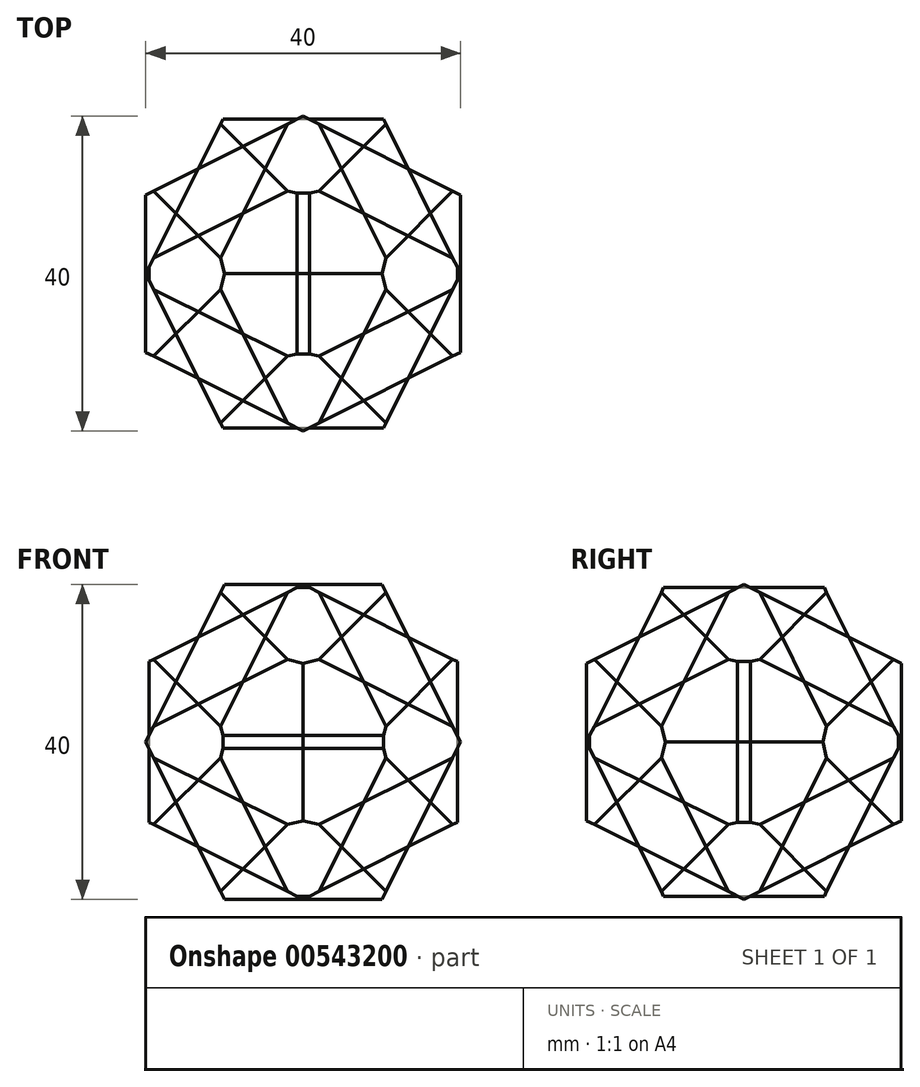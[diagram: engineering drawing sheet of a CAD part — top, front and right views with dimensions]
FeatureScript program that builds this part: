
annotation { "Feature Type Name" : "Feature", "Feature Type Description" : "" }
export const myFeature = defineFeature(function(context is Context, id is Id, definition is map)
    precondition{}
    {
        {
            var Q0;
            Q0=qCreatedBy(makeId("Front.planeOp"),FACE);
            var sketch = newSketch(context, id + "F0", { "sketchPlane" : qUnion([Q0])});
            skLineSegment(sketch, "E0", {"start": v(40, 0) * mm, "end": v(0, 20) * mm});
            skLineSegment(sketch, "E1", {"start": v(0, 20) * mm, "end": v(-40, 0) * mm});
            skLineSegment(sketch, "E2", {"start": v(-40, 0) * mm, "end": v(0, -20) * mm});
            skLineSegment(sketch, "E3", {"start": v(0, -20) * mm, "end": v(40, 0) * mm});
            skSolve(sketch);
        }
        {
            var Q0;
            Q0=makeQuery(id+"F0.imprint","IMPRINT",FACE,{"disambiguationData":[TD([[makeQuery(id+"F0.imprint","IMPRINT",EDGE,{"derivedFrom":sQuery(id+"F0.wireOp",EDGE,"E0")}),1.0]])]});
            extrude(context, id + "F1", {"entities" : qUnion([Q0]), "depth" : 25 * mm, "offsetDistance" : 25 * mm, "hasSecondDirection" : true, "secondDirectionOppositeDirection" : true, "secondDirectionDepth" : 25 * mm});
        }
        {
            var Q0;
            Q0=qCreatedBy(makeId("Front.planeOp"),FACE);
            var sketch = newSketch(context, id + "F2", { "sketchPlane" : qUnion([Q0])});
            skLineSegment(sketch, "E4", {"start": v(0, 49.78) * mm, "end": v(0, 0) * mm});
            skSolve(sketch);
        }
        {
            var Q0;
            Q0=qCreatedBy(makeId("Front.planeOp"),FACE);
            var sketch = newSketch(context, id + "F3", { "sketchPlane" : qUnion([Q0])});
            skLineSegment(sketch, "E5", {"start": v(60.84, 0) * mm, "end": v(0, 0) * mm});
            skSolve(sketch);
        }
        {
            var Q0;
            Q0=qCreatedBy(makeId("Right.planeOp"),FACE);
            var sketch = newSketch(context, id + "F4", { "sketchPlane" : qUnion([Q0])});
            skLineSegment(sketch, "E6", {"start": v(48.72, 0) * mm, "end": v(-1.84, 0) * mm});
            skSolve(sketch);
        }
        {
            var Q0;
            Q0=makeQuery(id+"F1.opExtrude","SWEPT_BODY",BODY,{"disambiguationData":[OSD([sQuery(id+"F0.wireOp",EDGE,"E0"),sQuery(id+"F0.wireOp",EDGE,"E1"),sQuery(id+"F0.wireOp",EDGE,"E2"),sQuery(id+"F0.wireOp",EDGE,"E3")])]});
            var Q1;
            Q1=sQuery(id+"F2.wireOp",EDGE,"E4");
            transform(context, id + "F5", {"entities" : qUnion([Q0]), "transformType" : TransformType.ROTATION, "transformAxis" : qUnion([Q1]), "angle" : 90 * degree, "makeCopy" : true});
        }
        {
            var Q0;
            Q0=makeQuery(id+"F5.opPattern","COPY",BODY,{"derivedFrom":makeQuery(id+"F1.opExtrude","SWEPT_BODY",BODY,{"disambiguationData":[OSD([sQuery(id+"F0.wireOp",EDGE,"E0"),sQuery(id+"F0.wireOp",EDGE,"E1"),sQuery(id+"F0.wireOp",EDGE,"E2"),sQuery(id+"F0.wireOp",EDGE,"E3")])]}),"instanceName":"1"});
            var Q1;
            Q1=sQuery(id+"F4.wireOp",EDGE,"E6");
            transform(context, id + "F6", {"entities" : qUnion([Q0]), "transformType" : TransformType.ROTATION, "transformAxis" : qUnion([Q1]), "angle" : 90 * degree, "makeCopy" : true});
        }
        {
            var Q0;
            Q0=makeQuery(id+"F5.opPattern","COPY",BODY,{"derivedFrom":makeQuery(id+"F1.opExtrude","SWEPT_BODY",BODY,{"disambiguationData":[OSD([sQuery(id+"F0.wireOp",EDGE,"E0"),sQuery(id+"F0.wireOp",EDGE,"E1"),sQuery(id+"F0.wireOp",EDGE,"E2"),sQuery(id+"F0.wireOp",EDGE,"E3")])]}),"instanceName":"1"});
            var Q1;
            Q1=sQuery(id+"F3.wireOp",EDGE,"E5");
            transform(context, id + "F7", {"entities" : qUnion([Q0]), "transformType" : TransformType.ROTATION, "transformAxis" : qUnion([Q1]), "angle" : 90 * degree, "makeCopy" : false});
        }
        {
            var Q0;
            Q0=makeQuery(id+"F5.opPattern","COPY",BODY,{"derivedFrom":makeQuery(id+"F1.opExtrude","SWEPT_BODY",BODY,{"disambiguationData":[OSD([sQuery(id+"F0.wireOp",EDGE,"E0"),sQuery(id+"F0.wireOp",EDGE,"E1"),sQuery(id+"F0.wireOp",EDGE,"E2"),sQuery(id+"F0.wireOp",EDGE,"E3")])]}),"instanceName":"1"});
            var Q1;
            Q1=makeQuery(id+"F6.opPattern","COPY",BODY,{"derivedFrom":makeQuery(id+"F5.opPattern","COPY",BODY,{"derivedFrom":makeQuery(id+"F1.opExtrude","SWEPT_BODY",BODY,{"disambiguationData":[OSD([sQuery(id+"F0.wireOp",EDGE,"E0"),sQuery(id+"F0.wireOp",EDGE,"E1"),sQuery(id+"F0.wireOp",EDGE,"E2"),sQuery(id+"F0.wireOp",EDGE,"E3")])]}),"instanceName":"1"}),"instanceName":"1"});
            booleanBodies(context, id + "F8", {"operationType" : BooleanOperationType.INTERSECTION, "tools" : qUnion([Q0, Q1])});
        }
        {
            var Q0;
            {var subQ0=makeQuery(id+"F5.opPattern","COPY",BODY,{"derivedFrom":makeQuery(id+"F1.opExtrude","SWEPT_BODY",BODY,{"disambiguationData":[OSD([sQuery(id+"F0.wireOp",EDGE,"E0"),sQuery(id+"F0.wireOp",EDGE,"E1"),sQuery(id+"F0.wireOp",EDGE,"E2"),sQuery(id+"F0.wireOp",EDGE,"E3")])]}),"instanceName":"1"});Q0=makeQuery(id+"F8.opBoolean","INTERSECT",BODY,{"derivedFrom":[subQ0,makeQuery(id+"F6.opPattern","COPY",BODY,{"derivedFrom":subQ0,"instanceName":"1"})]});}
            var Q1;
            Q1=makeQuery(id+"F1.opExtrude","SWEPT_BODY",BODY,{"disambiguationData":[OSD([sQuery(id+"F0.wireOp",EDGE,"E0"),sQuery(id+"F0.wireOp",EDGE,"E1"),sQuery(id+"F0.wireOp",EDGE,"E2"),sQuery(id+"F0.wireOp",EDGE,"E3")])]});
            booleanBodies(context, id + "F9", {"operationType" : BooleanOperationType.INTERSECTION, "tools" : qUnion([Q0, Q1])});
        }
        {
            var Q0;
            Q0=qCreatedBy(makeId("Top.planeOp"),FACE);
            var sketch = newSketch(context, id + "F10", { "sketchPlane" : qUnion([Q0])});
            skLineSegment(sketch, "E7", {"start": v(20, 0) * mm, "end": v(0, 20) * mm});
            skLineSegment(sketch, "E8", {"start": v(0, 20) * mm, "end": v(-20, 0) * mm});
            skLineSegment(sketch, "E9", {"start": v(-20, 0) * mm, "end": v(0, -20) * mm});
            skLineSegment(sketch, "E10", {"start": v(0, -20) * mm, "end": v(20, 0) * mm});
            skSolve(sketch);
        }
        {
            var Q0;
            Q0=qSketchRegion(id+"F10",true);
            extrude(context, id + "F11", {"entities" : qUnion([Q0]), "depth" : 20 * mm, "offsetDistance" : 25 * mm, "hasDraft" : true, "draftAngle" : atan(1 / sqrt(2)), "draftPullDirection" : true, "hasSecondDirection" : true, "secondDirectionOppositeDirection" : true, "secondDirectionDepth" : 20 * mm, "hasSecondDirectionDraft" : true, "secondDirectionDraftAngle" : atan(1 / sqrt(2)), "secondDirectionDraftPullDirection" : true});
        }
        {
            var Q0;
            {var subQ0=makeQuery(id+"F1.opExtrude","SWEPT_BODY",BODY,{"disambiguationData":[OSD([sQuery(id+"F0.wireOp",EDGE,"E0"),sQuery(id+"F0.wireOp",EDGE,"E1"),sQuery(id+"F0.wireOp",EDGE,"E2"),sQuery(id+"F0.wireOp",EDGE,"E3")])]});var subQ1=makeQuery(id+"F5.opPattern","COPY",BODY,{"derivedFrom":subQ0,"instanceName":"1"});Q0=makeQuery(id+"F9.opBoolean","INTERSECT",BODY,{"derivedFrom":[subQ0,makeQuery(id+"F8.opBoolean","INTERSECT",BODY,{"derivedFrom":[subQ1,makeQuery(id+"F6.opPattern","COPY",BODY,{"derivedFrom":subQ1,"instanceName":"1"})]})]});}
            transform(context, id + "F12", {"entities" : qUnion([Q0]), "transformType" : TransformType.TRANSLATION_3D, "dx" : 50 * mm, "dy" : 0 * mm, "dz" : 0 * mm, "makeCopy" : false});
        }
        {
            var Q0;
            Q0=makeQuery(id+"F11.*.split.splitOp","SPLIT",BODY,{"derivedFrom":makeQuery(id+"F11.opExtrude","SWEPT_BODY",BODY,{"disambiguationData":[OSD([sQuery(id+"F10.wireOp",EDGE,"E7"),sQuery(id+"F10.wireOp",EDGE,"E8"),sQuery(id+"F10.wireOp",EDGE,"E9"),sQuery(id+"F10.wireOp",EDGE,"E10")])]})});
            var Q1;
            Q1=qCreatedBy(makeId("Origin.pointOp"),VERTEX);
            transform(context, id + "F13", {"entities" : qUnion([Q0]), "transformType" : TransformType.SCALE_UNIFORMLY, "scale" : 1.5, "scalePoint" : qUnion([Q1]), "makeCopy" : false});
        }
        {
            var Q0;
            {var subQ0=makeQuery(id+"F1.opExtrude","SWEPT_BODY",BODY,{"disambiguationData":[OSD([sQuery(id+"F0.wireOp",EDGE,"E0"),sQuery(id+"F0.wireOp",EDGE,"E1"),sQuery(id+"F0.wireOp",EDGE,"E2"),sQuery(id+"F0.wireOp",EDGE,"E3")])]});var subQ1=makeQuery(id+"F5.opPattern","COPY",BODY,{"derivedFrom":subQ0,"instanceName":"1"});Q0=makeQuery(id+"F9.opBoolean","INTERSECT",BODY,{"derivedFrom":[subQ0,makeQuery(id+"F8.opBoolean","INTERSECT",BODY,{"derivedFrom":[subQ1,makeQuery(id+"F6.opPattern","COPY",BODY,{"derivedFrom":subQ1,"instanceName":"1"})]})]});}
            transform(context, id + "F14", {"entities" : qUnion([Q0]), "transformType" : TransformType.TRANSLATION_3D, "dx" : -50 * mm, "dy" : 0 * mm, "dz" : 0 * mm, "makeCopy" : false});
        }
        {
            var Q0;
            Q0=makeQuery(id+"F11.*.split.splitOp","SPLIT",BODY,{"derivedFrom":makeQuery(id+"F11.opExtrude","SWEPT_BODY",BODY,{"disambiguationData":[OSD([sQuery(id+"F10.wireOp",EDGE,"E7"),sQuery(id+"F10.wireOp",EDGE,"E8"),sQuery(id+"F10.wireOp",EDGE,"E9"),sQuery(id+"F10.wireOp",EDGE,"E10")])]})});
            var Q1;
            Q1=qCreatedBy(makeId("Origin.pointOp"),VERTEX);
            transform(context, id + "F15", {"entities" : qUnion([Q0]), "transformType" : TransformType.SCALE_UNIFORMLY, "scale" : 1.05, "scalePoint" : qUnion([Q1]), "makeCopy" : false});
        }
        {
            var Q0;
            Q0=makeQuery(id+"F11.*.split.splitOp","SPLIT",BODY,{"derivedFrom":makeQuery(id+"F11.opExtrude","SWEPT_BODY",BODY,{"disambiguationData":[OSD([sQuery(id+"F10.wireOp",EDGE,"E7"),sQuery(id+"F10.wireOp",EDGE,"E8"),sQuery(id+"F10.wireOp",EDGE,"E9"),sQuery(id+"F10.wireOp",EDGE,"E10")])]})});
            var Q1;
            {var subQ0=makeQuery(id+"F1.opExtrude","SWEPT_BODY",BODY,{"disambiguationData":[OSD([sQuery(id+"F0.wireOp",EDGE,"E0"),sQuery(id+"F0.wireOp",EDGE,"E1"),sQuery(id+"F0.wireOp",EDGE,"E2"),sQuery(id+"F0.wireOp",EDGE,"E3")])]});var subQ1=makeQuery(id+"F5.opPattern","COPY",BODY,{"derivedFrom":subQ0,"instanceName":"1"});Q1=makeQuery(id+"F9.opBoolean","INTERSECT",BODY,{"derivedFrom":[subQ0,makeQuery(id+"F8.opBoolean","INTERSECT",BODY,{"derivedFrom":[subQ1,makeQuery(id+"F6.opPattern","COPY",BODY,{"derivedFrom":subQ1,"instanceName":"1"})]})]});}
            booleanBodies(context, id + "F16", {"operationType" : BooleanOperationType.INTERSECTION, "tools" : qUnion([Q0, Q1])});
        }
        {
            var Q0;
            {var subQ0=makeQuery(id+"F1.opExtrude","SWEPT_BODY",BODY,{"disambiguationData":[OSD([sQuery(id+"F0.wireOp",EDGE,"E0"),sQuery(id+"F0.wireOp",EDGE,"E1"),sQuery(id+"F0.wireOp",EDGE,"E2"),sQuery(id+"F0.wireOp",EDGE,"E3")])]});var subQ1=makeQuery(id+"F5.opPattern","COPY",BODY,{"derivedFrom":subQ0,"instanceName":"1"});Q0=makeQuery(id+"F16.opBoolean","INTERSECT",BODY,{"derivedFrom":[makeQuery(id+"F9.opBoolean","INTERSECT",BODY,{"derivedFrom":[subQ0,makeQuery(id+"F8.opBoolean","INTERSECT",BODY,{"derivedFrom":[subQ1,makeQuery(id+"F6.opPattern","COPY",BODY,{"derivedFrom":subQ1,"instanceName":"1"})]})]}),makeQuery(id+"F11.*.split.splitOp","SPLIT",BODY,{"derivedFrom":makeQuery(id+"F11.opExtrude","SWEPT_BODY",BODY,{"disambiguationData":[OSD([sQuery(id+"F10.wireOp",EDGE,"E7"),sQuery(id+"F10.wireOp",EDGE,"E8"),sQuery(id+"F10.wireOp",EDGE,"E9"),sQuery(id+"F10.wireOp",EDGE,"E10")])]})})]});}
            var Q1;
            Q1=sQuery(id+"F2.wireOp",EDGE,"E4");
            transform(context, id + "F17", {"entities" : qUnion([Q0]), "transformType" : TransformType.ROTATION, "transformAxis" : qUnion([Q1]), "angle" : 90 * degree, "makeCopy" : true});
        }
        {
            var Q0;
            Q0=qCreatedBy(makeId("Top.planeOp"),FACE);
            var sketch = newSketch(context, id + "F18", { "sketchPlane" : qUnion([Q0])});
            skLineSegment(sketch, "E11", {"start": v(-20, -20) * mm, "end": v(20, -20) * mm});
            skLineSegment(sketch, "E12", {"start": v(20, -20) * mm, "end": v(20, 20) * mm});
            skLineSegment(sketch, "E13", {"start": v(20, 20) * mm, "end": v(-20, 20) * mm});
            skLineSegment(sketch, "E14", {"start": v(-20, 20) * mm, "end": v(-20, -20) * mm});
            skSolve(sketch);
        }
        {
            var Q0;
            Q0=makeQuery(id+"F18.imprint","IMPRINT",FACE,{"disambiguationData":[TD([[makeQuery(id+"F18.imprint","IMPRINT",EDGE,{"derivedFrom":sQuery(id+"F18.wireOp",EDGE,"E11")}),1.0]])]});
            extrude(context, id + "F19", {"entities" : qUnion([Q0]), "depth" : 20 * mm, "offsetDistance" : 25 * mm, "hasSecondDirection" : true, "secondDirectionOppositeDirection" : true, "secondDirectionDepth" : 20 * mm});
        }
        {
            var Q0;
            Q0=makeQuery(id+"F19.opExtrude","SWEPT_BODY",BODY,{"disambiguationData":[OSD([sQuery(id+"F18.wireOp",EDGE,"E11"),sQuery(id+"F18.wireOp",EDGE,"E12"),sQuery(id+"F18.wireOp",EDGE,"E13"),sQuery(id+"F18.wireOp",EDGE,"E14")])]});
            var Q1;
            Q1=sQuery(id+"F2.wireOp",VERTEX,"E4.end");
            transform(context, id + "F20", {"entities" : qUnion([Q0]), "transformType" : TransformType.SCALE_UNIFORMLY, "scale" : 0.98, "scalePoint" : qUnion([Q1]), "makeCopy" : false});
        }
        {
            var Q0;
            Q0=makeQuery(id+"F19.opExtrude","SWEPT_BODY",BODY,{"disambiguationData":[OSD([sQuery(id+"F18.wireOp",EDGE,"E11"),sQuery(id+"F18.wireOp",EDGE,"E12"),sQuery(id+"F18.wireOp",EDGE,"E13"),sQuery(id+"F18.wireOp",EDGE,"E14")])]});
            var Q1;
            {var subQ0=makeQuery(id+"F1.opExtrude","SWEPT_BODY",BODY,{"disambiguationData":[OSD([sQuery(id+"F0.wireOp",EDGE,"E0"),sQuery(id+"F0.wireOp",EDGE,"E1"),sQuery(id+"F0.wireOp",EDGE,"E2"),sQuery(id+"F0.wireOp",EDGE,"E3")])]});var subQ1=makeQuery(id+"F5.opPattern","COPY",BODY,{"derivedFrom":subQ0,"instanceName":"1"});Q1=makeQuery(id+"F16.opBoolean","INTERSECT",BODY,{"derivedFrom":[makeQuery(id+"F9.opBoolean","INTERSECT",BODY,{"derivedFrom":[subQ0,makeQuery(id+"F8.opBoolean","INTERSECT",BODY,{"derivedFrom":[subQ1,makeQuery(id+"F6.opPattern","COPY",BODY,{"derivedFrom":subQ1,"instanceName":"1"})]})]}),makeQuery(id+"F11.*.split.splitOp","SPLIT",BODY,{"derivedFrom":makeQuery(id+"F11.opExtrude","SWEPT_BODY",BODY,{"disambiguationData":[OSD([sQuery(id+"F10.wireOp",EDGE,"E7"),sQuery(id+"F10.wireOp",EDGE,"E8"),sQuery(id+"F10.wireOp",EDGE,"E9"),sQuery(id+"F10.wireOp",EDGE,"E10")])]})})]});}
            booleanBodies(context, id + "F21", {"operationType" : BooleanOperationType.INTERSECTION, "tools" : qUnion([Q0, Q1])});
        }
    });
